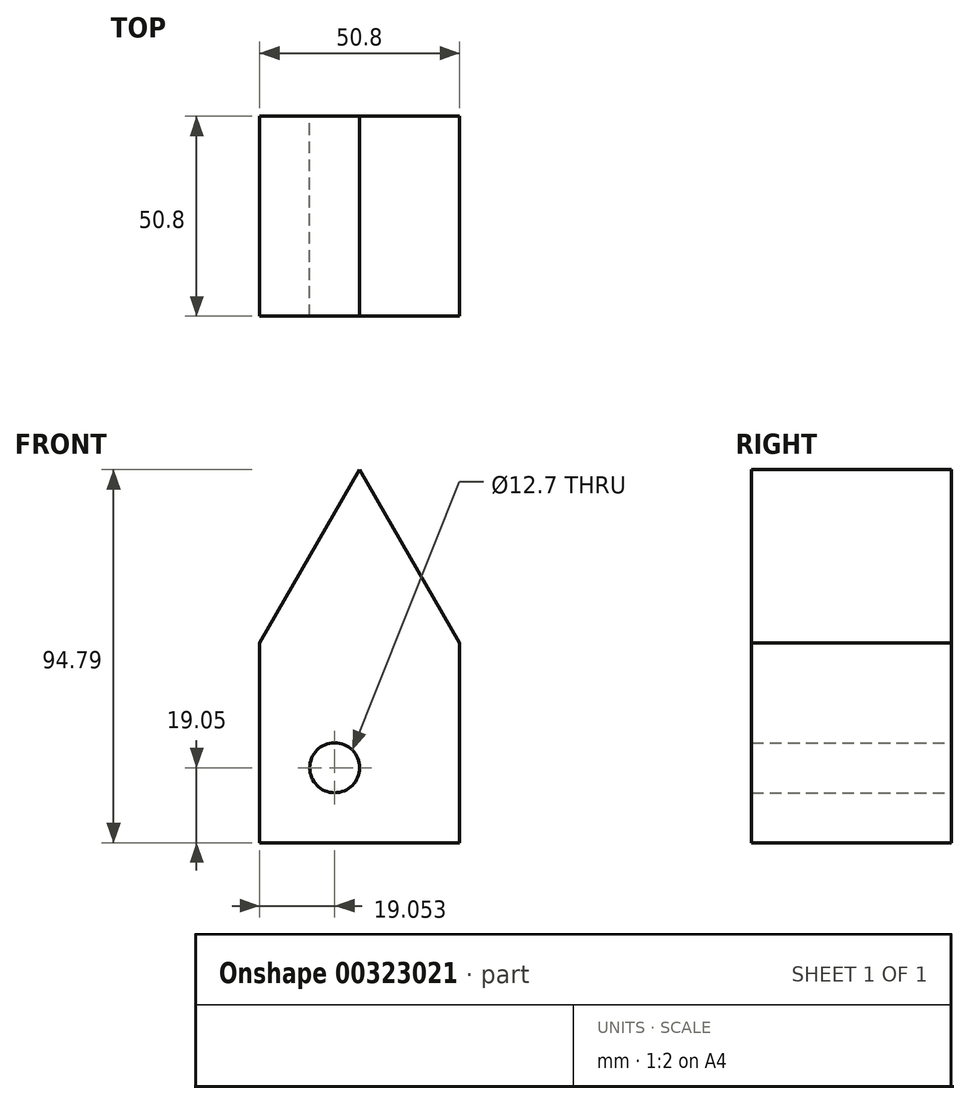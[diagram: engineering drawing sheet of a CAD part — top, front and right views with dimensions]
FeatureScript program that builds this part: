
annotation { "Feature Type Name" : "Feature", "Feature Type Description" : "" }
export const myFeature = defineFeature(function(context is Context, id is Id, definition is map)
    precondition{}
    {
        {
            var Q0;
            Q0=qCreatedBy(makeId("Front.planeOp"),FACE);
            var sketch = newSketch(context, id + "F0", { "sketchPlane" : qUnion([Q0])});
            skLineSegment(sketch, "E0.top", {"start": v(-24.4, -26.35) * mm, "end": v(26.4, -26.35) * mm});
            skLineSegment(sketch, "E0.left", {"start": v(-24.4, 24.45) * mm, "end": v(-24.4, -26.35) * mm});
            skLineSegment(sketch, "E0.right", {"start": v(26.4, 24.45) * mm, "end": v(26.4, -26.35) * mm});
            skLineSegment(sketch, "E1", {"start": v(-24.4, 24.45) * mm, "end": v(1, 68.44) * mm});
            skLineSegment(sketch, "E2", {"start": v(1, 68.44) * mm, "end": v(26.4, 24.45) * mm});
            skCircle(sketch, "E3", {"center": v(-5.35, -7.3) * mm, "radius": 6.35 * mm});
            skSolve(sketch);
        }
        {
            var Q0;
            Q0 = qSketchRegion(id + "F0", true);
            extrude(context, id + "F1", {"entities" : qUnion([Q0]), "depth" : 50.8 * mm});
        }
    });
